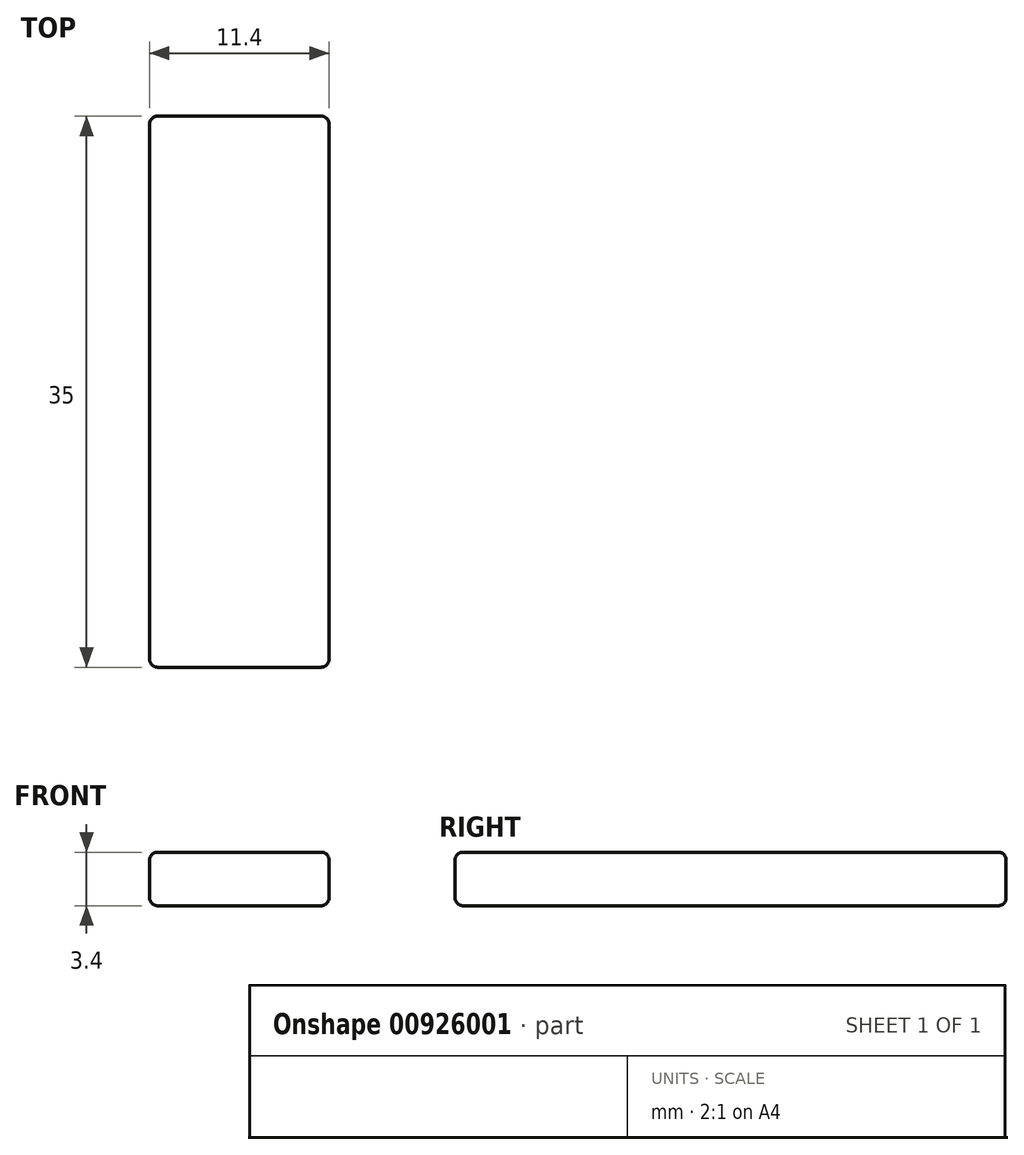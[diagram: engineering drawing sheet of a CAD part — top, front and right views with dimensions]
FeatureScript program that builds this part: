
annotation { "Feature Type Name" : "Feature", "Feature Type Description" : "" }
export const myFeature = defineFeature(function(context is Context, id is Id, definition is map)
    precondition{}
    {
        {
            var Q0;
            Q0=qCreatedBy(makeId("Front.planeOp"),FACE);
            var sketch = newSketch(context, id + "F0", { "sketchPlane" : qUnion([Q0])});
            skPoint(sketch, "E0.middle", {"position": v(0, 0) * mm});
            skPoint(sketch, "E1.bottom.end.orphan", {"position": v(-5, -35) * mm});
            skPoint(sketch, "E1.bottom.start.orphan", {"position": v(5, -35) * mm});
            skLineSegment(sketch, "E2.0", {"start": v(5.7, 1.7) * mm, "end": v(-5.7, 1.7) * mm});
            skLineSegment(sketch, "E2.1", {"start": v(5.7, 1.7) * mm, "end": v(5.7, -1.7) * mm});
            skLineSegment(sketch, "E2.2", {"start": v(5.7, -1.7) * mm, "end": v(-5.7, -1.7) * mm});
            skLineSegment(sketch, "E2.3", {"start": v(-5.7, 1.7) * mm, "end": v(-5.7, -1.7) * mm});
            skSolve(sketch);
        }
        {
            var Q0;
            Q0=makeQuery(id+"F0.imprint","IMPRINT",FACE,{"disambiguationData":[TD([[makeQuery(id+"F0.imprint","IMPRINT",EDGE,{"derivedFrom":sQuery(id+"F0.wireOp",EDGE,"E2.0")}),1.0]])]});
            extrude(context, id + "F1", {"entities" : qUnion([Q0]), "depth" : 35 * mm, "offsetDistance" : 25 * mm});
        }
        {
            var Q0;
            Q0=makeQuery(id+"F1.opExtrude","CAP_FACE",FACE,{"disambiguationData":[OSD([sQuery(id+"F0.wireOp",EDGE,"E2.0"),sQuery(id+"F0.wireOp",EDGE,"E2.1"),sQuery(id+"F0.wireOp",EDGE,"E2.2"),sQuery(id+"F0.wireOp",EDGE,"E2.3")])],"isStart":false});
            var Q1;
            Q1=makeQuery(id+"F1.opExtrude","SWEPT_FACE",FACE,{"disambiguationData":[OSD([sQuery(id+"F0.wireOp",EDGE,"E2.1")])]});
            var Q2;
            Q2=makeQuery(id+"F1.opExtrude","SWEPT_FACE",FACE,{"disambiguationData":[OSD([sQuery(id+"F0.wireOp",EDGE,"E2.3")])]});
            var Q3;
            Q3=makeQuery(id+"F1.opExtrude","CAP_FACE",FACE,{"disambiguationData":[OSD([sQuery(id+"F0.wireOp",EDGE,"E2.0"),sQuery(id+"F0.wireOp",EDGE,"E2.1"),sQuery(id+"F0.wireOp",EDGE,"E2.2"),sQuery(id+"F0.wireOp",EDGE,"E2.3")])],"isStart":true});
            var Q4;
            Q4=makeQuery(id+"F1.opExtrude","SWEPT_FACE",FACE,{"disambiguationData":[OSD([sQuery(id+"F0.wireOp",EDGE,"E2.0")])]});
            var Q5;
            Q5=makeQuery(id+"FBfamiLTMjm0Zoj_2.boolean.opBoolean","INTERSECT",EDGE,{"derivedFrom":[makeQuery(id+"F1.opExtrude","SWEPT_FACE",FACE,{"disambiguationData":[OSD([sQuery(id+"F0.wireOp",EDGE,"E2.2")])]}),makeQuery(id+"FBfamiLTMjm0Zoj_2.opExtrude","SWEPT_FACE",FACE,{"disambiguationData":[OSD([sQuery(id+"FgV9CzLMIjhU8uB_2.wireOp",EDGE,"JP4y15VA-6Ck7-CSWQ-tX4h-X0mHe9wyRXLq.right")])]})]});
            var Q6;
            Q6=makeQuery(id+"F1.opExtrude","SWEPT_FACE",FACE,{"disambiguationData":[OSD([sQuery(id+"F0.wireOp",EDGE,"E2.2")])]});
            fillet(context, id + "F2", {"entities" : qUnion([Q0, Q1, Q2, Q3, Q4, Q5, Q6]), "radius" : 0.5 * mm, "tangentPropagation" : true, "allowEdgeOverflow" : false});
        }
    });
